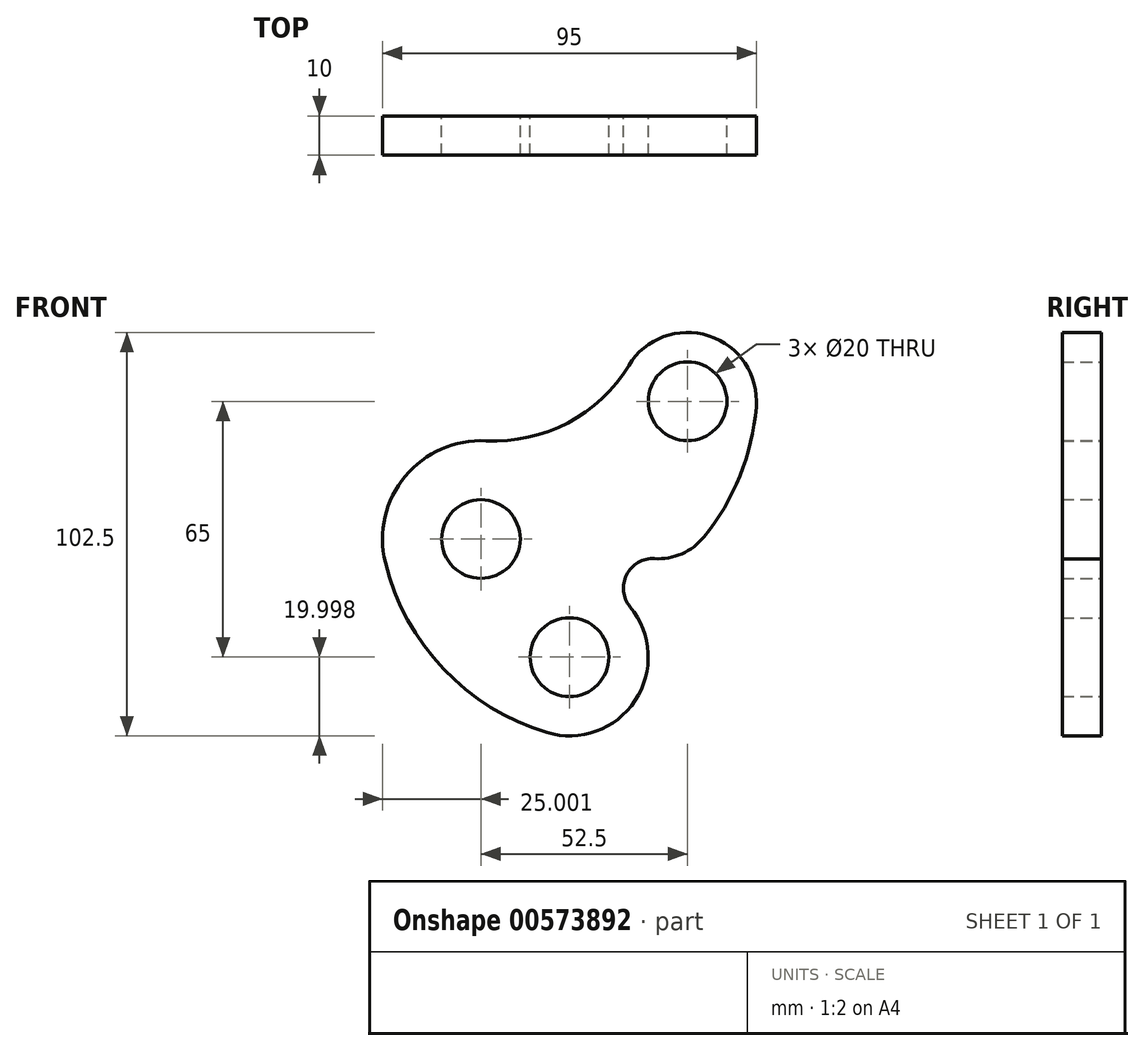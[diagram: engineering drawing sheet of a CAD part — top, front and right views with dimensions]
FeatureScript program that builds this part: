
annotation { "Feature Type Name" : "Feature", "Feature Type Description" : "" }
export const myFeature = defineFeature(function(context is Context, id is Id, definition is map)
    precondition{}
    {
        {
            var Q0;
            Q0=qCreatedBy(makeId("Front.planeOp"),FACE);
            var sketch = newSketch(context, id + "F0", { "sketchPlane" : qUnion([Q0])});
            skCircle(sketch, "E0", {"center": v(-34, -8.31) * mm, "radius": 10 * mm});
            skCircle(sketch, "E1", {"center": v(-11.5, -38.31) * mm, "radius": 10 * mm});
            skCircle(sketch, "E2", {"center": v(18.5, 26.69) * mm, "radius": 10 * mm});
            skArc(sketch, "E3", {"start": v(-58.28, -14.25) * mm, "mid": v(-43.51, -41.31) * mm, "end": v(-17.25, -57.47) * mm});
            skArc(sketch, "E4", {"start": v(-58.28, -14.25) * mm, "mid": v(-53.25, 7.63) * mm, "end": v(-32.7, 16.65) * mm});
            skArc(sketch, "E5", {"start": v(-32.7, 16.65) * mm, "mid": v(-11.93, 21.23) * mm, "end": v(3.56, 35.8) * mm});
            skArc(sketch, "E6", {"start": v(3.56, 35.8) * mm, "mid": v(23.91, 43.33) * mm, "end": v(35.94, 25.26) * mm});
            skArc(sketch, "E7", {"start": v(-17.25, -57.47) * mm, "mid": v(5.17, -49.36) * mm, "end": v(3.9, -25.56) * mm});
            skArc(sketch, "E8", {"start": v(10.12, -13.29) * mm, "mid": v(3, -17.38) * mm, "end": v(3.9, -25.56) * mm});
            skArc(sketch, "E9", {"start": v(35.94, 25.26) * mm, "mid": v(31.8, 7.72) * mm, "end": v(22.62, -7.8) * mm});
            skArc(sketch, "E10", {"start": v(22.62, -7.8) * mm, "mid": v(17.03, -12.05) * mm, "end": v(10.12, -13.29) * mm});
            skSolve(sketch);
        }
        {
            var Q0;
            Q0 = qSketchRegion(id + "F0", true);
            extrude(context, id + "F1", {"entities" : qUnion([Q0]), "depth" : 10 * mm, "offsetDistance" : 25 * mm});
        }
    });
